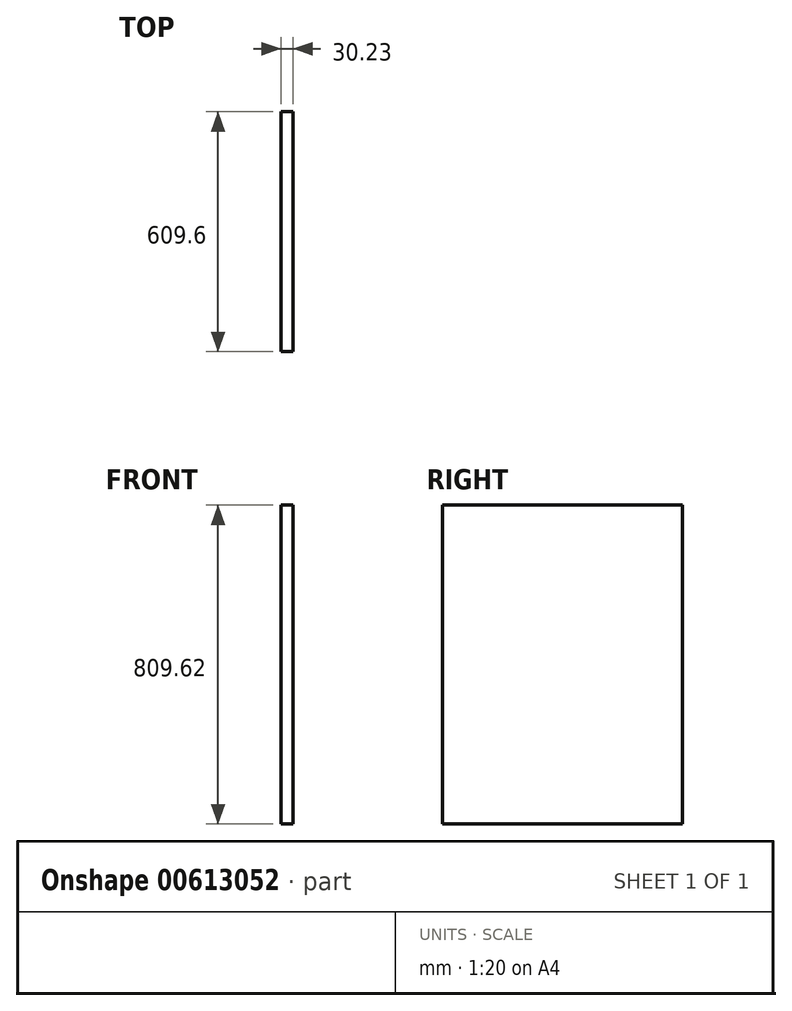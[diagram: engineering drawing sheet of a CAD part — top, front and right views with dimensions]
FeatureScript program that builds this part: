
annotation { "Feature Type Name" : "Feature", "Feature Type Description" : "" }
export const myFeature = defineFeature(function(context is Context, id is Id, definition is map)
    precondition{}
    {
        {
            var Q0;
            Q0=qCreatedBy(makeId("Right.planeOp"),FACE);
            var sketch = newSketch(context, id + "F0", { "sketchPlane" : qUnion([Q0])});
            skLineSegment(sketch, "E0.bottom", {"start": v(304.8, 404.81) * mm, "end": v(-304.8, 404.81) * mm});
            skLineSegment(sketch, "E0.top", {"start": v(304.8, -404.81) * mm, "end": v(-304.8, -404.81) * mm});
            skLineSegment(sketch, "E0.left", {"start": v(304.8, 404.81) * mm, "end": v(304.8, -404.81) * mm});
            skLineSegment(sketch, "E0.right", {"start": v(-304.8, 404.81) * mm, "end": v(-304.8, -404.81) * mm});
            skPoint(sketch, "E0.middle", {"position": v(0, 0) * mm});
            skSolve(sketch);
        }
        {
            var Q0;
            Q0=makeQuery(id+"F0.imprint","IMPRINT",FACE,{"disambiguationData":[TD([[makeQuery(id+"F0.imprint","IMPRINT",EDGE,{"derivedFrom":sQuery(id+"F0.wireOp",EDGE,"E0.bottom")}),1.0]])]});
            extrude(context, id + "F1", {"entities" : qUnion([Q0]), "depth" : 30.23 * mm, "offsetDistance" : 25.4 * mm});
        }
    });
